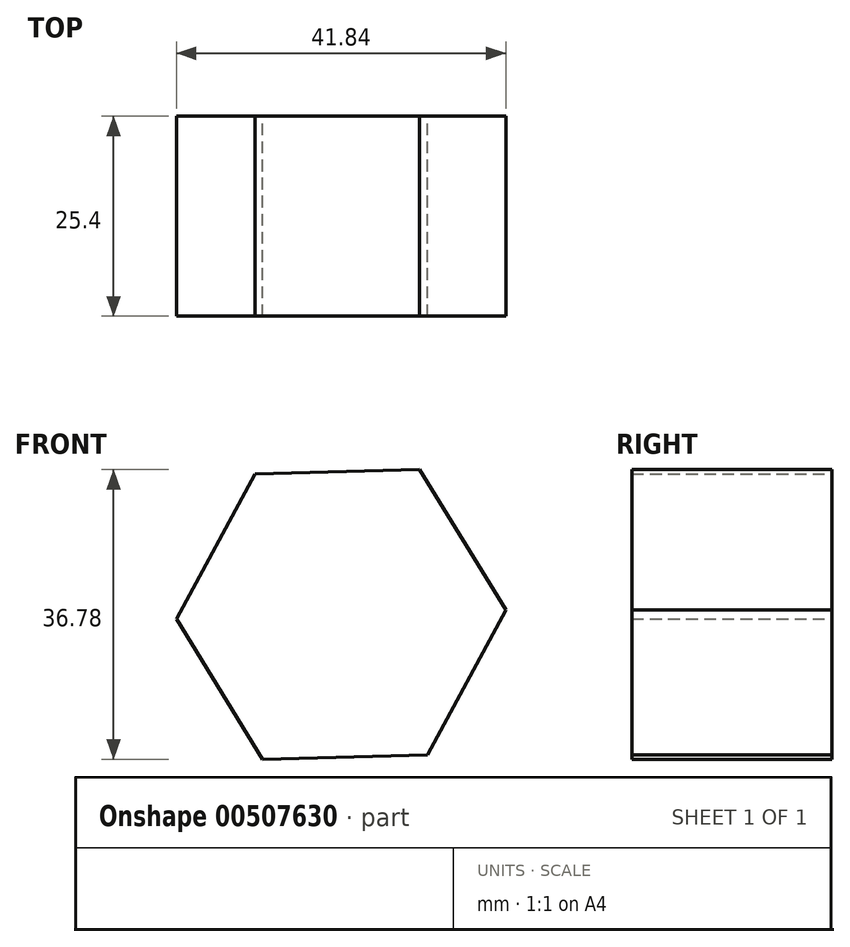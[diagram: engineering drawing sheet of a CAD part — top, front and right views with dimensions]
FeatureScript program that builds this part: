
annotation { "Feature Type Name" : "Feature", "Feature Type Description" : "" }
export const myFeature = defineFeature(function(context is Context, id is Id, definition is map)
    precondition{}
    {
        {
            var Q0;
            Q0=qCreatedBy(makeId("Front.planeOp"),FACE);
            var sketch = newSketch(context, id + "F0", { "sketchPlane" : qUnion([Q0])});
            skCircle(sketch, "E0.cCircle", {"center": v(0, 0) * mm, "radius": 18.12 * mm, "construction": true});
            skLineSegment(sketch, "E0.0", {"start": v(-9.98, -18.4) * mm, "end": v(-20.92, -0.55) * mm});
            skLineSegment(sketch, "E0.1", {"start": v(-20.92, -0.55) * mm, "end": v(-10.94, 17.84) * mm});
            skLineSegment(sketch, "E0.2", {"start": v(-10.94, 17.84) * mm, "end": v(9.98, 18.4) * mm});
            skLineSegment(sketch, "E0.3", {"start": v(9.98, 18.4) * mm, "end": v(20.92, 0.55) * mm});
            skLineSegment(sketch, "E0.4", {"start": v(20.92, 0.55) * mm, "end": v(10.94, -17.84) * mm});
            skLineSegment(sketch, "E0.5", {"start": v(10.94, -17.84) * mm, "end": v(-9.98, -18.4) * mm});
            skPoint(sketch, "E0.0.midPoint", {"position": v(-15.45, -9.47) * mm});
            skSolve(sketch);
        }
        {
            var Q0;
            Q0=makeQuery(id+"F0.imprint","IMPRINT",FACE,{"disambiguationData":[TD([[makeQuery(id+"F0.imprint","IMPRINT",EDGE,{"derivedFrom":sQuery(id+"F0.wireOp",EDGE,"E0.0")}),-1.0]])]});
            extrude(context, id + "F1", {"entities" : qUnion([Q0]), "endBound" : BoundingType.SYMMETRIC, "depth" : 25.4 * mm});
        }
    });
